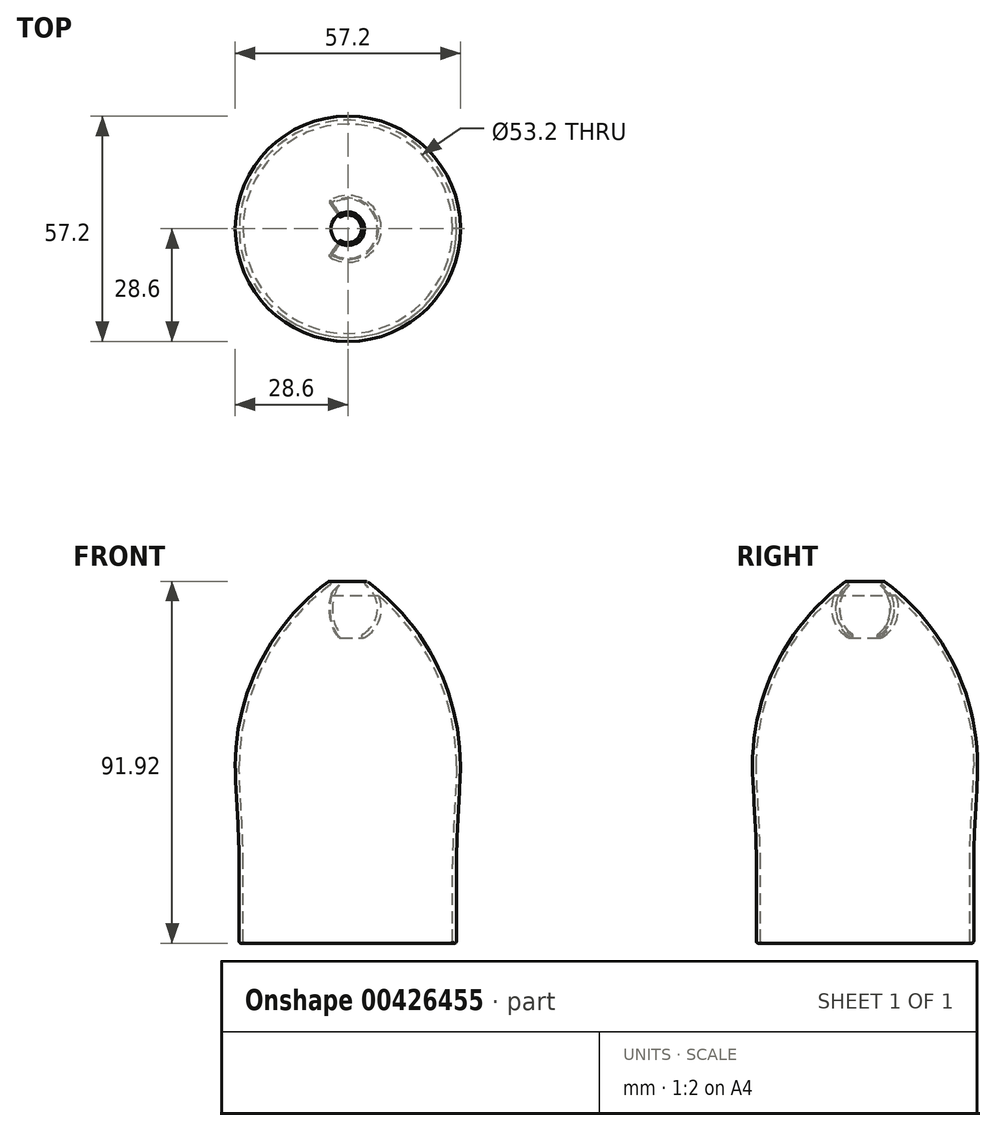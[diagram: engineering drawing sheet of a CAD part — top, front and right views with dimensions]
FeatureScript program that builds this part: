
annotation { "Feature Type Name" : "Feature", "Feature Type Description" : "" }
export const myFeature = defineFeature(function(context is Context, id is Id, definition is map)
    precondition{}
    {
        {
            var Q0;
            Q0=qCreatedBy(makeId("Top.planeOp"),FACE);
            var sketch = newSketch(context, id + "F0", { "sketchPlane" : qUnion([Q0])});
            skCircle(sketch, "E0", {"center": v(0, 0) * mm, "radius": 27.6 * mm});
            skCircle(sketch, "E1.0", {"center": v(0, 0) * mm, "radius": 28.6 * mm});
            skSolve(sketch);
        }
        {
            var Q0;
            Q0=qCreatedBy(makeId("Front.planeOp"),FACE);
            var sketch = newSketch(context, id + "F1", { "sketchPlane" : qUnion([Q0])});
            skCircle(sketch, "E2", {"center": v(0, 40) * mm, "radius": 7.5 * mm});
            skLineSegment(sketch, "E3", {"start": v(0, 40) * mm, "end": v(0, 0) * mm, "construction": true});
            skCircle(sketch, "E4.0", {"center": v(0, 40) * mm, "radius": 8.5 * mm, "construction": true});
            skSolve(sketch);
        }
        {
            var Q0;
            Q0=qCreatedBy(makeId("Top.planeOp"),FACE);
            cPlane(context, id + "F2", {"entities" : qUnion([Q0]), "cplaneType" : CPlaneType.OFFSET, "offset" : 25 * mm, "oppositeDirection" : true, "width" : 150 * mm, "height" : 150 * mm});
        }
        {
            var Q0;
            Q0=qCreatedBy(id+"F2.planeOp",FACE);
            var sketch = newSketch(context, id + "F3", { "sketchPlane" : qUnion([Q0])});
            skCircle(sketch, "E5", {"center": v(0, 0) * mm, "radius": 27.6 * mm});
            skCircle(sketch, "E6.0", {"center": v(0, 0) * mm, "radius": 28.6 * mm, "construction": true});
            skCircle(sketch, "E7.0", {"center": v(0, 0) * mm, "radius": 26.6 * mm});
            skSolve(sketch);
        }
        {
            var Q0;
            Q0 = qSketchRegion(id + "F1", true);
            var sketch = newSketch(context, id + "F4", { "sketchPlane" : qUnion([Q0])});
            skArc(sketch, "E8", {"start": v(5.07, 46.82) * mm, "mid": v(4.37, 46.72) * mm, "end": v(4.48, 46.02) * mm});
            skLineSegment(sketch, "E9", {"start": v(-27.6, 0) * mm, "end": v(-28.6, 0) * mm});
            skArc(sketch, "E10", {"start": v(5.07, 46.82) * mm, "mid": v(22.39, 26.2) * mm, "end": v(28.6, 0) * mm});
            skArc(sketch, "E11", {"start": v(27.6, 0) * mm, "mid": v(21.5, 25.75) * mm, "end": v(4.48, 46.02) * mm});
            skLineSegment(sketch, "E12", {"start": v(28.6, 0) * mm, "end": v(27.6, 0) * mm});
            skLineSegment(sketch, "E13", {"start": v(-26.6, -25) * mm, "end": v(-27.6, -25) * mm});
            skLineSegment(sketch, "E14", {"start": v(27.6, -25) * mm, "end": v(26.6, -25) * mm});
            skLineSegment(sketch, "E15", {"start": v(26.6, -25) * mm, "end": v(26.6, -45) * mm});
            skLineSegment(sketch, "E16", {"start": v(26.6, -45) * mm, "end": v(27.6, -45) * mm});
            skLineSegment(sketch, "E17", {"start": v(27.6, -45) * mm, "end": v(27.6, -25) * mm});
            skFitSpline(sketch, "E18", {"points": [v(28.6, 0) * mm, v(27.6, -25) * mm], "startDerivative": vector(0, -15.32) * mm, "endDerivative": vector(0, -27.65) * mm});
            skFitSpline(sketch, "E19", {"points": [v(27.6, 0) * mm, v(26.6, -25) * mm], "startDerivative": vector(0, -15.32) * mm, "endDerivative": vector(0, -27.65) * mm});
            skLineSegment(sketch, "E20", {"start": v(28.6, 0) * mm, "end": v(28.6, -5.1) * mm, "construction": true});
            skLineSegment(sketch, "E21", {"start": v(27.6, 0) * mm, "end": v(27.6, -5.1) * mm, "construction": true});
            skSolve(sketch);
        }
        {
            var Q0;
            Q0=qCreatedBy(makeId("Front.planeOp"),FACE);
            var sketch = newSketch(context, id + "F5", { "sketchPlane" : qUnion([Q0])});
            skArc(sketch, "E22.0", {"start": v(4.25, 32.64) * mm, "mid": v(8.06, 37.3) * mm, "end": v(7.82, 43.33) * mm});
            skArc(sketch, "E23.0", {"start": v(3.75, 33.5) * mm, "mid": v(7.49, 39.57) * mm, "end": v(4.48, 46.02) * mm});
            skLineSegment(sketch, "E24", {"start": v(0, 40) * mm, "end": v(4.25, 32.64) * mm, "construction": true});
            skArc(sketch, "E25", {"start": v(3.75, 33.5) * mm, "mid": v(3.57, 32.82) * mm, "end": v(4.25, 32.64) * mm});
            skArc(sketch, "E26.0", {"start": v(7.82, 43.33) * mm, "mid": v(6.17, 44.7) * mm, "end": v(4.48, 46.02) * mm});
            skPoint(sketch, "E27.orphan", {"position": v(27.6, 0) * mm});
            skSolve(sketch);
        }
        {
            var Q0;
            Q0 = qSketchRegion(id + "F5", true);
            var Q1;
            Q1=sQuery(id+"F1.wireOp",EDGE,"E3");
            revolve(context, id + "F6", {"entities" : qUnion([Q0]), "axis" : qUnion([Q1]), "revolveType" : RevolveType.SYMMETRIC, "angle" : 250 * degree});
        }
        {
            var Q0;
            Q0 = qSketchRegion(id + "F4", true);
            var Q1;
            Q1=sQuery(id+"F1.wireOp",EDGE,"E3");
            revolve(context, id + "F7", {"operationType" : NewBodyOperationType.ADD, "entities" : qUnion([Q0]), "axis" : qUnion([Q1]), "revolveType" : RevolveType.FULL});
        }
        {
            var Q0;
            Q0=makeQuery(id+"F6.opRevolve","CAP_EDGE",EDGE,{"disambiguationData":[OSD([sQuery(id+"F5.wireOp",EDGE,"E22.0")])],"isStart":true});
            var Q1;
            Q1=makeQuery(id+"F6.opRevolve","CAP_EDGE",EDGE,{"disambiguationData":[OSD([sQuery(id+"F5.wireOp",EDGE,"E22.0")])],"isStart":false});
            fillet(context, id + "F8", {"entities" : qUnion([Q0, Q1]), "radius" : 0.5 * mm, "tangentPropagation" : true, "allowEdgeOverflow" : false});
        }
        {
            var Q0;
            Q0=makeQuery(id+"F7.opRevolve","SWEPT_FACE",FACE,{"disambiguationData":[OSD([sQuery(id+"F4.wireOp",EDGE,"E16")])]});
            fillet(context, id + "F9", {"entities" : qUnion([Q0]), "radius" : 0.5 * mm, "tangentPropagation" : true, "allowEdgeOverflow" : false});
        }
    });
